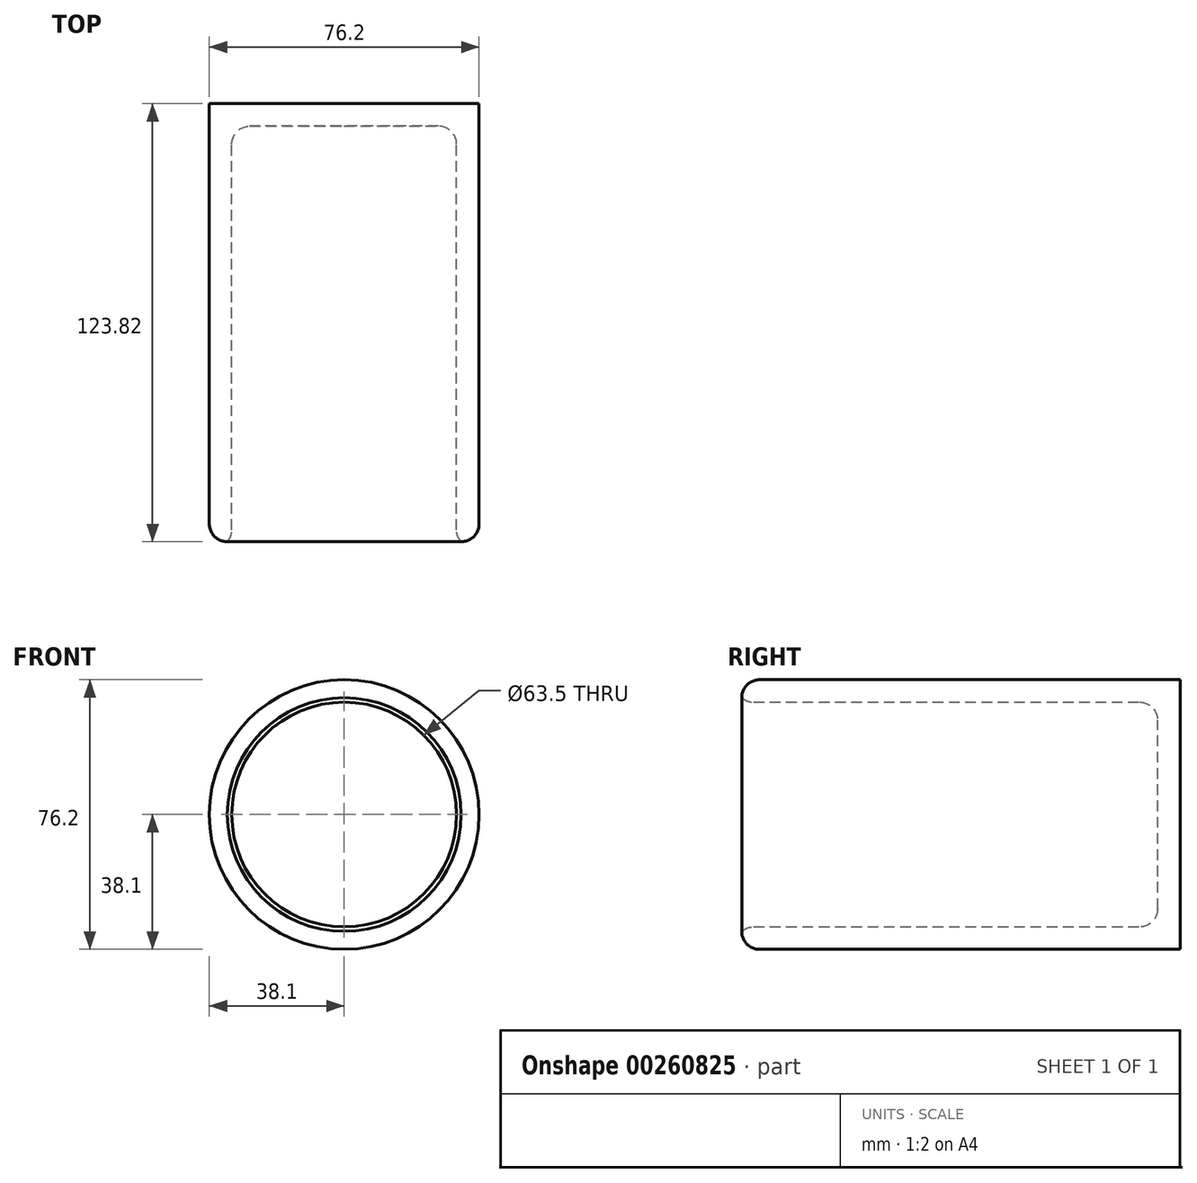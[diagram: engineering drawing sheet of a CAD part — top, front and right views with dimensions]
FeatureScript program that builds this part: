
annotation { "Feature Type Name" : "Feature", "Feature Type Description" : "" }
export const myFeature = defineFeature(function(context is Context, id is Id, definition is map)
    precondition{}
    {
        {
            var Q0;
            Q0=qCreatedBy(makeId("Front.planeOp"),FACE);
            var sketch = newSketch(context, id + "F0", { "sketchPlane" : qUnion([Q0])});
            skCircle(sketch, "E0", {"center": v(0, 0) * mm, "radius": 38.1 * mm});
            skSolve(sketch);
        }
        {
            var Q0;
            Q0=makeQuery(id+"F0.imprint","IMPRINT",FACE,{"disambiguationData":[TD([[makeQuery(id+"F0.imprint","IMPRINT",EDGE,{"derivedFrom":sQuery(id+"F0.wireOp",EDGE,"E0")}),1.0]])]});
            extrude(context, id + "F1", {"entities" : qUnion([Q0]), "endBound" : BoundingType.SYMMETRIC, "depth" : 123.82 * mm});
        }
        {
            var Q0;
            Q0=makeQuery(id+"F1.opExtrude","CAP_EDGE",EDGE,{"disambiguationData":[OSD([sQuery(id+"F0.wireOp",EDGE,"E0")])],"isStart":false});
            fillet(context, id + "F2", {"entities" : qUnion([Q0]), "radius" : 5.08 * mm, "tangentPropagation" : true, "allowEdgeOverflow" : false});
        }
        {
            var Q0;
            Q0=makeQuery(id+"F1.opExtrude","CAP_FACE",FACE,{"disambiguationData":[OSD([sQuery(id+"F0.wireOp",EDGE,"E0")])],"isStart":false});
            shell(context, id + "F3", {"entities" : qUnion([Q0]), "thickness" : 6.35 * mm});
        }
        {
            var Q0;
            {var subQ0=sQuery(id+"F0.wireOp",EDGE,"E0");Q0=makeQuery(id+"F2.opFillet","BLEND_EDGE",EDGE,{"blendedFrom":[makeQuery(id+"F1.opExtrude","CAP_EDGE",EDGE,{"disambiguationData":[OSD([subQ0])],"isStart":false}),makeQuery(id+"F1.opExtrude","CAP_FACE",FACE,{"disambiguationData":[OSD([subQ0])],"isStart":false})],"blendedInto":[makeQuery(id+"F1.opExtrude","CAP_FACE",FACE,{"disambiguationData":[OSD([subQ0])],"isStart":false})]});}
            var Q1;
            {var subQ0=sQuery(id+"F0.wireOp",EDGE,"E0");var subQ1=makeQuery(id+"F1.opExtrude","CAP_EDGE",EDGE,{"disambiguationData":[OSD([subQ0])],"isStart":false});Q1=makeQuery(id+"F3.opShell","OFFSET_EDGE",EDGE,{"disambiguationData":[OSD([subQ0]),TDD([makeQuery(id+"F2.opFillet","BLEND_EDGE",EDGE,{"blendedFrom":[subQ1,makeQuery(id+"F1.opExtrude","SWEPT_FACE",FACE,{"disambiguationData":[OSD([subQ0])]})],"blendedInto":[makeQuery(id+"F1.opExtrude","SWEPT_FACE",FACE,{"disambiguationData":[OSD([subQ0])]})]}),makeQuery(id+"F2.opFillet","BLEND_EDGE",EDGE,{"blendedFrom":[subQ1,makeQuery(id+"F1.opExtrude","CAP_FACE",FACE,{"disambiguationData":[OSD([subQ0])],"isStart":false})],"blendedInto":[makeQuery(id+"F1.opExtrude","CAP_FACE",FACE,{"disambiguationData":[OSD([subQ0])],"isStart":false})]})])]});}
            var Q2;
            {var subQ0=sQuery(id+"F0.wireOp",EDGE,"E0");Q2=makeQuery(id+"F3.opShell","OFFSET_FACE",FACE,{"disambiguationData":[OSD([subQ0]),TDD([makeQuery(id+"F1.opExtrude","SWEPT_FACE",FACE,{"disambiguationData":[OSD([subQ0])]})])]});}
            fillet(context, id + "F4", {"entities" : qUnion([Q0, Q1, Q2]), "radius" : 5.08 * mm, "tangentPropagation" : true, "allowEdgeOverflow" : false});
        }
    });
